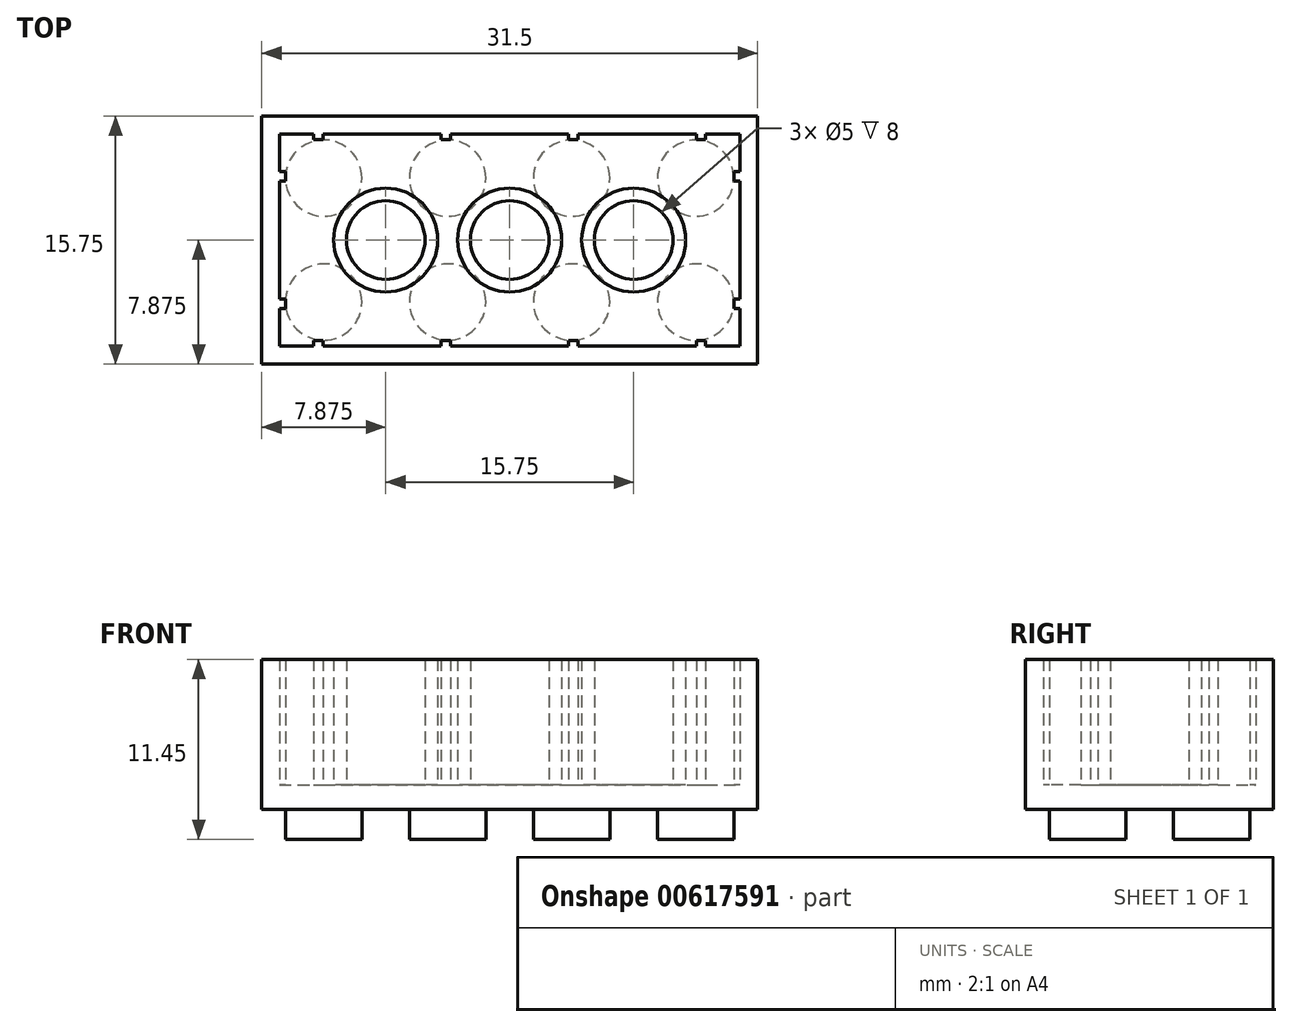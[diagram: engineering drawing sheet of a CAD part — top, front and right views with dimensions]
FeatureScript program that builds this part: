
annotation { "Feature Type Name" : "Feature", "Feature Type Description" : "" }
export const myFeature = defineFeature(function(context is Context, id is Id, definition is map)
    precondition{}
    {
        {
            var Q0;
            Q0=qCreatedBy(makeId("Top.planeOp"),FACE);
            var sketch = newSketch(context, id + "F0", { "sketchPlane" : qUnion([Q0])});
            skLineSegment(sketch, "E0", {"start": v(-31.5, 0) * mm, "end": v(-31.5, 15.75) * mm});
            skLineSegment(sketch, "E1", {"start": v(-31.5, 15.75) * mm, "end": v(0, 15.75) * mm});
            skLineSegment(sketch, "E2", {"start": v(0, 15.75) * mm, "end": v(0, 0) * mm});
            skLineSegment(sketch, "E3", {"start": v(0, 0) * mm, "end": v(-31.5, 0) * mm});
            skLineSegment(sketch, "E4.0", {"start": v(-30.37, 14.62) * mm, "end": v(-1.13, 14.62) * mm});
            skLineSegment(sketch, "E4.1", {"start": v(-30.37, 1.13) * mm, "end": v(-30.37, 14.62) * mm});
            skLineSegment(sketch, "E4.2", {"start": v(-1.13, 1.13) * mm, "end": v(-30.37, 1.13) * mm});
            skLineSegment(sketch, "E4.3", {"start": v(-1.13, 14.62) * mm, "end": v(-1.13, 1.13) * mm});
            skLineSegment(sketch, "E5", {"start": v(-28.2, 14.62) * mm, "end": v(-28.2, 14.25) * mm});
            skLineSegment(sketch, "E6", {"start": v(-28.2, 14.25) * mm, "end": v(-27.6, 14.25) * mm});
            skLineSegment(sketch, "E7", {"start": v(-27.6, 14.25) * mm, "end": v(-27.6, 14.62) * mm});
            skLineSegment(sketch, "E8", {"start": v(-20.1, 14.62) * mm, "end": v(-20.1, 14.25) * mm});
            skLineSegment(sketch, "E9", {"start": v(-20.1, 14.25) * mm, "end": v(-19.5, 14.25) * mm});
            skLineSegment(sketch, "E10", {"start": v(-19.5, 14.25) * mm, "end": v(-19.5, 14.62) * mm});
            skLineSegment(sketch, "E11", {"start": v(-30.37, 12.23) * mm, "end": v(-30, 12.23) * mm});
            skLineSegment(sketch, "E12", {"start": v(-30, 12.23) * mm, "end": v(-30, 11.63) * mm});
            skLineSegment(sketch, "E13", {"start": v(-30, 11.63) * mm, "end": v(-30.37, 11.63) * mm});
            skLineSegment(sketch, "E14", {"start": v(-30.37, 3.52) * mm, "end": v(-30, 3.52) * mm});
            skLineSegment(sketch, "E15", {"start": v(-30, 3.53) * mm, "end": v(-30, 4.12) * mm});
            skLineSegment(sketch, "E16", {"start": v(-30, 4.12) * mm, "end": v(-30.37, 4.12) * mm});
            skLineSegment(sketch, "E17", {"start": v(-12, 1.13) * mm, "end": v(-12, 1.5) * mm});
            skLineSegment(sketch, "E18", {"start": v(-12, 1.5) * mm, "end": v(-11.4, 1.5) * mm});
            skLineSegment(sketch, "E19", {"start": v(-11.4, 1.5) * mm, "end": v(-11.4, 1.13) * mm});
            skLineSegment(sketch, "E20", {"start": v(-3.9, 1.13) * mm, "end": v(-3.9, 1.5) * mm});
            skLineSegment(sketch, "E21", {"start": v(-3.9, 1.5) * mm, "end": v(-3.3, 1.5) * mm});
            skLineSegment(sketch, "E22", {"start": v(-3.3, 1.5) * mm, "end": v(-3.3, 1.13) * mm});
            skLineSegment(sketch, "E23", {"start": v(-1.13, 12.23) * mm, "end": v(-1.5, 12.23) * mm});
            skLineSegment(sketch, "E24", {"start": v(-1.5, 12.23) * mm, "end": v(-1.5, 11.62) * mm});
            skLineSegment(sketch, "E25", {"start": v(-1.5, 11.63) * mm, "end": v(-1.13, 11.63) * mm});
            skLineSegment(sketch, "E26", {"start": v(-1.13, 3.52) * mm, "end": v(-1.5, 3.52) * mm});
            skLineSegment(sketch, "E27", {"start": v(-1.5, 3.53) * mm, "end": v(-1.5, 4.13) * mm});
            skLineSegment(sketch, "E28", {"start": v(-1.5, 4.12) * mm, "end": v(-1.13, 4.12) * mm});
            skLineSegment(sketch, "E29", {"start": v(-31.5, 7.87) * mm, "end": v(0, 7.88) * mm, "construction": true});
            skLineSegment(sketch, "E30", {"start": v(-15.75, 15.75) * mm, "end": v(-15.75, 0) * mm, "construction": true});
            skLineSegment(sketch, "E31", {"start": v(-19.5, 1.13) * mm, "end": v(-19.5, 1.5) * mm});
            skLineSegment(sketch, "E32", {"start": v(-19.5, 1.5) * mm, "end": v(-20.1, 1.5) * mm});
            skLineSegment(sketch, "E33", {"start": v(-20.1, 1.5) * mm, "end": v(-20.1, 1.13) * mm});
            skLineSegment(sketch, "E34", {"start": v(-27.6, 1.13) * mm, "end": v(-27.6, 1.5) * mm});
            skLineSegment(sketch, "E35", {"start": v(-27.6, 1.5) * mm, "end": v(-28.2, 1.5) * mm});
            skLineSegment(sketch, "E36", {"start": v(-28.2, 1.5) * mm, "end": v(-28.2, 1.13) * mm});
            skLineSegment(sketch, "E37", {"start": v(-12, 14.62) * mm, "end": v(-12, 14.25) * mm});
            skLineSegment(sketch, "E38", {"start": v(-12, 14.25) * mm, "end": v(-11.4, 14.25) * mm});
            skLineSegment(sketch, "E39", {"start": v(-11.4, 14.25) * mm, "end": v(-11.4, 14.62) * mm});
            skLineSegment(sketch, "E40", {"start": v(-3.9, 14.62) * mm, "end": v(-3.9, 14.25) * mm});
            skLineSegment(sketch, "E41", {"start": v(-3.9, 14.25) * mm, "end": v(-3.3, 14.25) * mm});
            skLineSegment(sketch, "E42", {"start": v(-3.3, 14.25) * mm, "end": v(-3.3, 14.62) * mm});
            skLineSegment(sketch, "E43", {"start": v(-31.5, 0) * mm, "end": v(-15.75, 15.75) * mm, "construction": true});
            skLineSegment(sketch, "E44", {"start": v(-15.75, 15.75) * mm, "end": v(0, 0) * mm, "construction": true});
            skCircle(sketch, "E45", {"center": v(-23.63, 7.87) * mm, "radius": 3.3 * mm});
            skCircle(sketch, "E46", {"center": v(-7.88, 7.88) * mm, "radius": 3.3 * mm});
            skCircle(sketch, "E47.0", {"center": v(-23.63, 7.87) * mm, "radius": 2.5 * mm});
            skCircle(sketch, "E48.0", {"center": v(-7.88, 7.88) * mm, "radius": 2.5 * mm});
            skCircle(sketch, "E49", {"center": v(-15.75, 7.88) * mm, "radius": 3.3 * mm});
            skCircle(sketch, "E50.0", {"center": v(-15.75, 7.88) * mm, "radius": 2.5 * mm});
            skSolve(sketch);
        }
        {
            var Q0;
            Q0=makeQuery(id+"F0.imprint","IMPRINT",FACE,{"disambiguationData":[TD([[makeQuery(id+"F0.imprint","IMPRINT",EDGE,{"derivedFrom":sQuery(id+"F0.wireOp",EDGE,"E0")}),-1.0]])]});
            var Q1;
            {var subQ0=sQuery(id+"F0.wireOp",EDGE,"E11");Q1=makeQuery(id+"F0.imprint","IMPRINT",FACE,{"disambiguationData":[TD([[makeQuery(id+"F0.imprint","IMPRINT",EDGE,{"derivedFrom":subQ0}),-1.0]])]});}
            var Q2;
            {var subQ0=sQuery(id+"F0.wireOp",EDGE,"E5");Q2=makeQuery(id+"F0.imprint","IMPRINT",FACE,{"disambiguationData":[TD([[makeQuery(id+"F0.imprint","IMPRINT",EDGE,{"derivedFrom":subQ0}),1.0]])]});}
            var Q3;
            {var subQ0=sQuery(id+"F0.wireOp",EDGE,"E8");Q3=makeQuery(id+"F0.imprint","IMPRINT",FACE,{"disambiguationData":[TD([[makeQuery(id+"F0.imprint","IMPRINT",EDGE,{"derivedFrom":subQ0}),1.0]])]});}
            var Q4;
            {var subQ0=sQuery(id+"F0.wireOp",EDGE,"E37");Q4=makeQuery(id+"F0.imprint","IMPRINT",FACE,{"disambiguationData":[TD([[makeQuery(id+"F0.imprint","IMPRINT",EDGE,{"derivedFrom":subQ0}),1.0]])]});}
            var Q5;
            {var subQ0=sQuery(id+"F0.wireOp",EDGE,"E40");Q5=makeQuery(id+"F0.imprint","IMPRINT",FACE,{"disambiguationData":[TD([[makeQuery(id+"F0.imprint","IMPRINT",EDGE,{"derivedFrom":subQ0}),1.0]])]});}
            var Q6;
            {var subQ0=sQuery(id+"F0.wireOp",EDGE,"E23");Q6=makeQuery(id+"F0.imprint","IMPRINT",FACE,{"disambiguationData":[TD([[makeQuery(id+"F0.imprint","IMPRINT",EDGE,{"derivedFrom":subQ0}),1.0]])]});}
            var Q7;
            {var subQ0=sQuery(id+"F0.wireOp",EDGE,"E26");Q7=makeQuery(id+"F0.imprint","IMPRINT",FACE,{"disambiguationData":[TD([[makeQuery(id+"F0.imprint","IMPRINT",EDGE,{"derivedFrom":subQ0}),-1.0]])]});}
            var Q8;
            {var subQ0=sQuery(id+"F0.wireOp",EDGE,"E20");Q8=makeQuery(id+"F0.imprint","IMPRINT",FACE,{"disambiguationData":[TD([[makeQuery(id+"F0.imprint","IMPRINT",EDGE,{"derivedFrom":subQ0}),-1.0]])]});}
            var Q9;
            {var subQ0=sQuery(id+"F0.wireOp",EDGE,"E17");Q9=makeQuery(id+"F0.imprint","IMPRINT",FACE,{"disambiguationData":[TD([[makeQuery(id+"F0.imprint","IMPRINT",EDGE,{"derivedFrom":subQ0}),-1.0]])]});}
            var Q10;
            {var subQ0=sQuery(id+"F0.wireOp",EDGE,"E31");Q10=makeQuery(id+"F0.imprint","IMPRINT",FACE,{"disambiguationData":[TD([[makeQuery(id+"F0.imprint","IMPRINT",EDGE,{"derivedFrom":subQ0}),1.0]])]});}
            var Q11;
            {var subQ0=sQuery(id+"F0.wireOp",EDGE,"E34");Q11=makeQuery(id+"F0.imprint","IMPRINT",FACE,{"disambiguationData":[TD([[makeQuery(id+"F0.imprint","IMPRINT",EDGE,{"derivedFrom":subQ0}),1.0]])]});}
            var Q12;
            {var subQ0=sQuery(id+"F0.wireOp",EDGE,"E14");Q12=makeQuery(id+"F0.imprint","IMPRINT",FACE,{"disambiguationData":[TD([[makeQuery(id+"F0.imprint","IMPRINT",EDGE,{"derivedFrom":subQ0}),1.0]])]});}
            var Q13;
            Q13=makeQuery(id+"F0.imprint","IMPRINT",FACE,{"disambiguationData":[TD([[makeQuery(id+"F0.imprint","IMPRINT",EDGE,{"derivedFrom":sQuery(id+"F0.wireOp",EDGE,"RC2XXzG0-cfXw-t4KE-vMmq-h9YtXDcDc6rl")}),1.0]])]});
            var Q14;
            Q14=makeQuery(id+"F0.imprint","IMPRINT",FACE,{"disambiguationData":[TD([[makeQuery(id+"F0.imprint","IMPRINT",EDGE,{"derivedFrom":sQuery(id+"F0.wireOp",EDGE,"p31WC0DB-rjj7-IxBY-orDS-cudCZ7p6vhk8")}),1.0]])]});
            var Q15;
            Q15=makeQuery(id+"F0.imprint","IMPRINT",FACE,{"disambiguationData":[TD([[makeQuery(id+"F0.imprint","IMPRINT",EDGE,{"derivedFrom":sQuery(id+"F0.wireOp",EDGE,"E45")}),1.0]])]});
            var Q16;
            Q16=makeQuery(id+"F0.imprint","IMPRINT",FACE,{"disambiguationData":[TD([[makeQuery(id+"F0.imprint","IMPRINT",EDGE,{"derivedFrom":sQuery(id+"F0.wireOp",EDGE,"E46")}),1.0]])]});
            var Q17;
            Q17=makeQuery(id+"F0.imprint","IMPRINT",FACE,{"disambiguationData":[TD([[makeQuery(id+"F0.imprint","IMPRINT",EDGE,{"derivedFrom":sQuery(id+"F0.wireOp",EDGE,"E49")}),1.0]])]});
            extrude(context, id + "F1", {"entities" : qUnion([Q0, Q1, Q2, Q3, Q4, Q5, Q6, Q7, Q8, Q9, Q10, Q11, Q12, Q13, Q14, Q15, Q16, Q17]), "depth" : 9.55 * mm, "offsetDistance" : 25 * mm});
        }
        {
            var Q0;
            {var subQ24=sQuery(id+"F0.wireOp",EDGE,"E5");Q0=makeQuery(id+"F0.imprint","IMPRINT",FACE,{"disambiguationData":[TD([[makeQuery(id+"F0.imprint","IMPRINT",EDGE,{"derivedFrom":subQ24}),-1.0]])]});}
            var Q1;
            Q1=makeQuery(id+"F0.imprint","IMPRINT",FACE,{"disambiguationData":[TD([[makeQuery(id+"F0.imprint","IMPRINT",EDGE,{"derivedFrom":sQuery(id+"F0.wireOp",EDGE,"28f55383-3981-4276-91bd-8ed36bddb3cb.0")}),1.0]])]});
            var Q2;
            Q2=makeQuery(id+"F0.imprint","IMPRINT",FACE,{"disambiguationData":[TD([[makeQuery(id+"F0.imprint","IMPRINT",EDGE,{"derivedFrom":sQuery(id+"F0.wireOp",EDGE,"7d87069b-ef7a-4ec5-9948-4a517cb3c2a5.0")}),1.0]])]});
            var Q3;
            Q3=makeQuery(id+"F0.imprint","IMPRINT",FACE,{"disambiguationData":[TD([[makeQuery(id+"F0.imprint","IMPRINT",EDGE,{"derivedFrom":sQuery(id+"F0.wireOp",EDGE,"E47.0")}),1.0]])]});
            var Q4;
            Q4=makeQuery(id+"F0.imprint","IMPRINT",FACE,{"disambiguationData":[TD([[makeQuery(id+"F0.imprint","IMPRINT",EDGE,{"derivedFrom":sQuery(id+"F0.wireOp",EDGE,"E48.0")}),1.0]])]});
            var Q5;
            Q5=makeQuery(id+"F0.imprint","IMPRINT",FACE,{"disambiguationData":[TD([[makeQuery(id+"F0.imprint","IMPRINT",EDGE,{"derivedFrom":sQuery(id+"F0.wireOp",EDGE,"E50.0")}),1.0]])]});
            extrude(context, id + "F2", {"entities" : qUnion([Q0, Q1, Q2, Q3, Q4, Q5]), "operationType" : NewBodyOperationType.ADD, "depth" : 1.55 * mm, "offsetDistance" : 25 * mm});
        }
        {
            var Q0;
            Q0=makeQuery(id+"F0.imprint","IMPRINT",FACE,{"disambiguationData":[TD([[makeQuery(id+"F0.imprint","IMPRINT",EDGE,{"derivedFrom":sQuery(id+"F0.wireOp",EDGE,"E0")}),-1.0]])]});
            var sketch = newSketch(context, id + "F3", { "sketchPlane" : qUnion([Q0])});
            skLineSegment(sketch, "E51.bottom", {"start": v(0, 0) * mm, "end": v(-31.5, 0) * mm});
            skLineSegment(sketch, "E51.top", {"start": v(0, 15.75) * mm, "end": v(-31.5, 15.75) * mm});
            skLineSegment(sketch, "E51.left", {"start": v(0, 0) * mm, "end": v(0, 15.75) * mm});
            skLineSegment(sketch, "E51.right", {"start": v(-31.5, 0) * mm, "end": v(-31.5, 15.75) * mm});
            skLineSegment(sketch, "E52", {"start": v(-31.5, 7.88) * mm, "end": v(0, 7.88) * mm, "construction": true});
            skLineSegment(sketch, "E53", {"start": v(-31.5, 0) * mm, "end": v(-15.75, 0) * mm, "construction": true});
            skLineSegment(sketch, "E54", {"start": v(-15.75, 0) * mm, "end": v(0, 0) * mm, "construction": true});
            skLineSegment(sketch, "E55", {"start": v(-23.62, 0) * mm, "end": v(-23.62, 15.75) * mm, "construction": true});
            skLineSegment(sketch, "E56", {"start": v(-7.88, 0) * mm, "end": v(-7.88, 15.75) * mm, "construction": true});
            skLineSegment(sketch, "E57", {"start": v(-31.5, 0) * mm, "end": v(-23.62, 7.88) * mm, "construction": true});
            skLineSegment(sketch, "E58", {"start": v(-23.62, 7.88) * mm, "end": v(-15.75, 15.75) * mm, "construction": true});
            skLineSegment(sketch, "E59", {"start": v(-15.75, 15.75) * mm, "end": v(-7.88, 7.88) * mm, "construction": true});
            skLineSegment(sketch, "E60", {"start": v(-7.88, 7.88) * mm, "end": v(0, 0) * mm, "construction": true});
            skLineSegment(sketch, "E61", {"start": v(0, 15.75) * mm, "end": v(-7.88, 7.88) * mm, "construction": true});
            skLineSegment(sketch, "E62", {"start": v(-15.75, 0) * mm, "end": v(-7.88, 7.88) * mm, "construction": true});
            skLineSegment(sketch, "E63", {"start": v(-15.75, 0) * mm, "end": v(-23.62, 7.88) * mm, "construction": true});
            skLineSegment(sketch, "E64", {"start": v(-23.62, 7.88) * mm, "end": v(-31.5, 15.75) * mm, "construction": true});
            skCircle(sketch, "E65", {"center": v(-27.56, 3.94) * mm, "radius": 2.43 * mm});
            skCircle(sketch, "E66", {"center": v(-19.69, 3.94) * mm, "radius": 2.43 * mm});
            skCircle(sketch, "E67", {"center": v(-27.56, 11.81) * mm, "radius": 2.43 * mm});
            skCircle(sketch, "E68", {"center": v(-19.69, 11.81) * mm, "radius": 2.43 * mm});
            skCircle(sketch, "E69", {"center": v(-11.81, 3.94) * mm, "radius": 2.43 * mm});
            skCircle(sketch, "E70", {"center": v(-11.81, 11.81) * mm, "radius": 2.43 * mm});
            skCircle(sketch, "E71", {"center": v(-3.94, 11.81) * mm, "radius": 2.43 * mm});
            skCircle(sketch, "E72", {"center": v(-3.94, 3.94) * mm, "radius": 2.43 * mm});
            skSolve(sketch);
        }
        {
            var Q0;
            Q0=makeQuery(id+"F3.imprint","IMPRINT",FACE,{"disambiguationData":[TD([[makeQuery(id+"F3.imprint","IMPRINT",EDGE,{"derivedFrom":sQuery(id+"F3.wireOp",EDGE,"E65")}),1.0]])]});
            var Q1;
            Q1=makeQuery(id+"F3.imprint","IMPRINT",FACE,{"disambiguationData":[TD([[makeQuery(id+"F3.imprint","IMPRINT",EDGE,{"derivedFrom":sQuery(id+"F3.wireOp",EDGE,"E69")}),1.0]])]});
            var Q2;
            Q2=makeQuery(id+"F3.imprint","IMPRINT",FACE,{"disambiguationData":[TD([[makeQuery(id+"F3.imprint","IMPRINT",EDGE,{"derivedFrom":sQuery(id+"F3.wireOp",EDGE,"E72")}),1.0]])]});
            var Q3;
            Q3=makeQuery(id+"F3.imprint","IMPRINT",FACE,{"disambiguationData":[TD([[makeQuery(id+"F3.imprint","IMPRINT",EDGE,{"derivedFrom":sQuery(id+"F3.wireOp",EDGE,"E71")}),1.0]])]});
            var Q4;
            Q4=makeQuery(id+"F3.imprint","IMPRINT",FACE,{"disambiguationData":[TD([[makeQuery(id+"F3.imprint","IMPRINT",EDGE,{"derivedFrom":sQuery(id+"F3.wireOp",EDGE,"E70")}),1.0]])]});
            var Q5;
            Q5=makeQuery(id+"F3.imprint","IMPRINT",FACE,{"disambiguationData":[TD([[makeQuery(id+"F3.imprint","IMPRINT",EDGE,{"derivedFrom":sQuery(id+"F3.wireOp",EDGE,"E68")}),1.0]])]});
            var Q6;
            Q6=makeQuery(id+"F3.imprint","IMPRINT",FACE,{"disambiguationData":[TD([[makeQuery(id+"F3.imprint","IMPRINT",EDGE,{"derivedFrom":sQuery(id+"F3.wireOp",EDGE,"E67")}),1.0]])]});
            var Q7;
            Q7=makeQuery(id+"F3.imprint","IMPRINT",FACE,{"disambiguationData":[TD([[makeQuery(id+"F3.imprint","IMPRINT",EDGE,{"derivedFrom":sQuery(id+"F3.wireOp",EDGE,"E66")}),1.0]])]});
            extrude(context, id + "F4", {"entities" : qUnion([Q0, Q1, Q2, Q3, Q4, Q5, Q6, Q7]), "operationType" : NewBodyOperationType.ADD, "oppositeDirection" : true, "depth" : 1.9 * mm, "offsetDistance" : 25 * mm});
        }
    });
